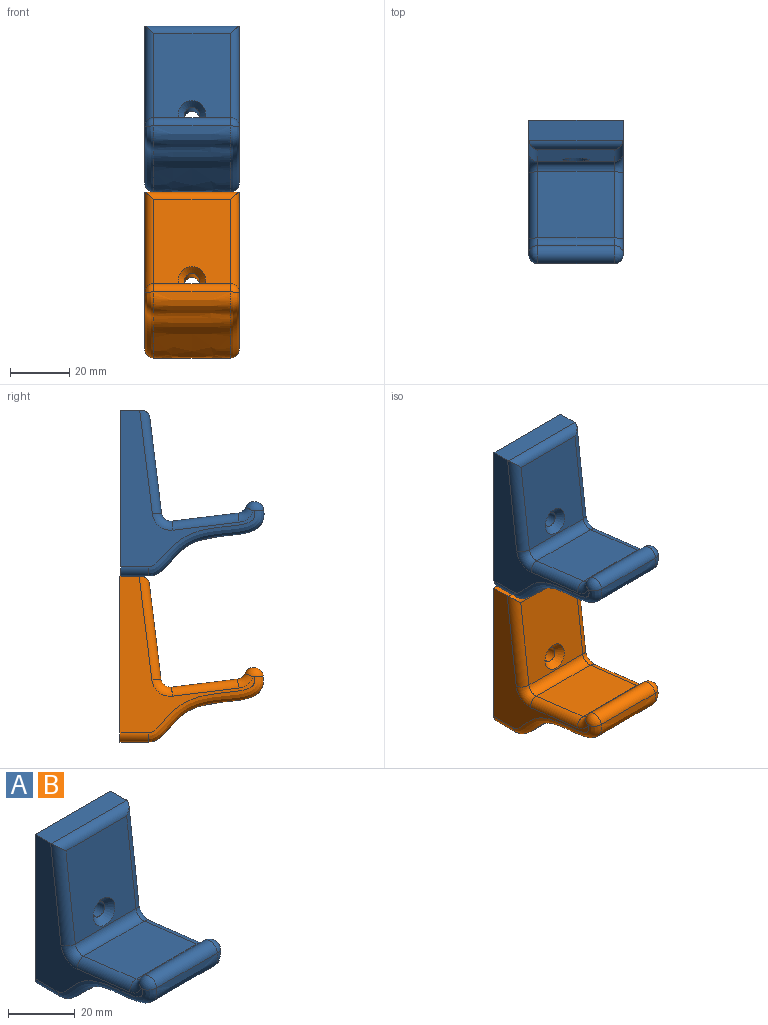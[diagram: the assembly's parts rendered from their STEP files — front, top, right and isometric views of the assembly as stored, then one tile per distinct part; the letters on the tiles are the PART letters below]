
ASSEMBLY  parts=2 mates=1
PART A: 37 faces, bbox 35.4x53.5x59.9 mm
  f0: plane 17.29x17.17mm, normal (0,1,0), area 174.1mm2, adj f12,f36
  f1: plane 31.99x25.65mm, normal (0,-0.99,0.12), area 761.5mm2, adj f7,f13,f20,f21,f22
  f2: plane 25.65x22.22mm, normal (0,0.12,0.99), area 574.4mm2, adj f7,f8,f18,f24
  f3: cylinder r=3.2mm len=25.65mm, axis (-1,0,0), area 215mm2, adj f4,f8,f16,f26
  f4: extruded ~38.76x25.65mm, area 1238mm2, adj f3,f9,f15,f27
  f5: plane 52.84x45.26mm, normal (1,0,0), area 608.4mm2, adj f10,f11,f22,f23,f24,f25,f26,f27
  f6: plane 52.84x45.26mm, normal (-1,0,0), area 608.4mm2, adj f10,f11,f14,f15,f16,f17,f18,f19
  f7: cylinder r=3.17mm len=25.65mm, axis (1,0,0), area 127.9mm2, adj f1,f2,f19,f23
  f8: cylinder r=3.17mm len=25.65mm, axis (-1,0,0), area 85.5mm2, adj f2,f3,f17,f25
  f9: plane 25.65x9.53mm, normal (0,0,-1), area 244.4mm2, adj f4,f10,f14,f28
  f10: plane 55.88x31.75mm, normal (0,1,0), area 817mm2, adj f5,f6,f9,f11,f14,f28,f31,f32
  f11: plane 31.75x6.83mm, normal (0,0,1), area 216.8mm2, adj f5,f6,f10,f20,f21,f22
  f12: cylinder r=2.49mm len=11.71mm, axis (0,-0.99,0.12), area 170.2mm2, adj f0,f13
  f13: cone r=2.49mm half-angle=41deg, axis (0,-0.99,0.12), area 69.9mm2, adj f1,f12
  f14: cylinder r=3.05mm len=9.59mm, axis (0,1,0), area 45.8mm2, adj f6,f9,f10,f15
  f15: bspline ~38.9x22.46mm, area 222mm2, adj f4,f6,f14,f16
  f16: torus R=0.15mm, axis (1,0,0), area 26.5mm2, adj f3,f6,f15,f17
  f17: torus R=6.22mm, axis (1,0,0), area 21.5mm2, adj f6,f8,f16,f18
  f18: cylinder r=3.05mm len=22.59mm, axis (0,-0.99,0.12), area 107.2mm2, adj f2,f6,f17,f19
  f19: torus R=6.22mm, axis (1,0,0), area 32.2mm2, adj f6,f7,f18,f20
  f20: cylinder r=3.05mm len=35.41mm, axis (0,-0.12,-0.99), area 163.6mm2, adj f1,f6,f11,f19,f21
  f21: cylinder r=3.05mm len=31.7mm, axis (1,0,0), area 126.6mm2, adj f1,f11,f20,f22
  f22: cylinder r=3.05mm len=35.41mm, axis (0,0.12,0.99), area 163.6mm2, adj f1,f5,f11,f21,f23
  f23: torus R=6.22mm, axis (1,0,0), area 32.2mm2, adj f5,f7,f22,f24
  f24: cylinder r=3.05mm len=22.59mm, axis (0,0.99,-0.12), area 107.2mm2, adj f2,f5,f23,f25
  f25: torus R=6.22mm, axis (1,0,0), area 21.5mm2, adj f5,f8,f24,f26
  f26: torus R=0.15mm, axis (1,0,0), area 26.5mm2, adj f3,f5,f25,f27
  f27: bspline ~38.94x22.64mm, area 222mm2, adj f4,f5,f26,f28
  f28: cylinder r=3.05mm len=9.59mm, axis (0,-1,0), area 45.8mm2, adj f5,f9,f10,f27
  f29: extruded ~21.08x7.87mm, area 233.9mm2, adj f31,f32,f33,f34
  f30: plane 29.98x21.08mm, normal (0,0.99,-0.12), area 467.2mm2, adj f31,f32,f33,f35,f36
  f31: plane 48.83x21.11mm, normal (-1,0,0), area 383.2mm2, adj f10,f29,f30,f33,f34,f35
  f32: plane 48.83x21.11mm, normal (1,0,0), area 383.2mm2, adj f10,f29,f30,f33,f34,f35
  f33: cylinder r=8.51mm len=21.08mm, axis (1,0,0), area 248.7mm2, adj f29,f30,f31,f32,f36
  f34: plane 21.08x9.62mm, normal (0,0,1), area 202.8mm2, adj f10,f29,f31,f32
  f35: plane 21.08x4.81mm, normal (0,0,-1), area 101.3mm2, adj f10,f30,f31,f32
  f36: cylinder r=7.82mm len=16.57mm, axis (0,-0.99,0.12), area 381.4mm2, adj f0,f30,f33
PART B: same geometry as A
PLACE A t=(42,-128.47,94.72)mm
PLACE B t=(42,-128.3,38.84)mm
MATE planar A.f9 <-> B.f11  axis (0,0,-1) through (42,-123.71,76.66)mm
